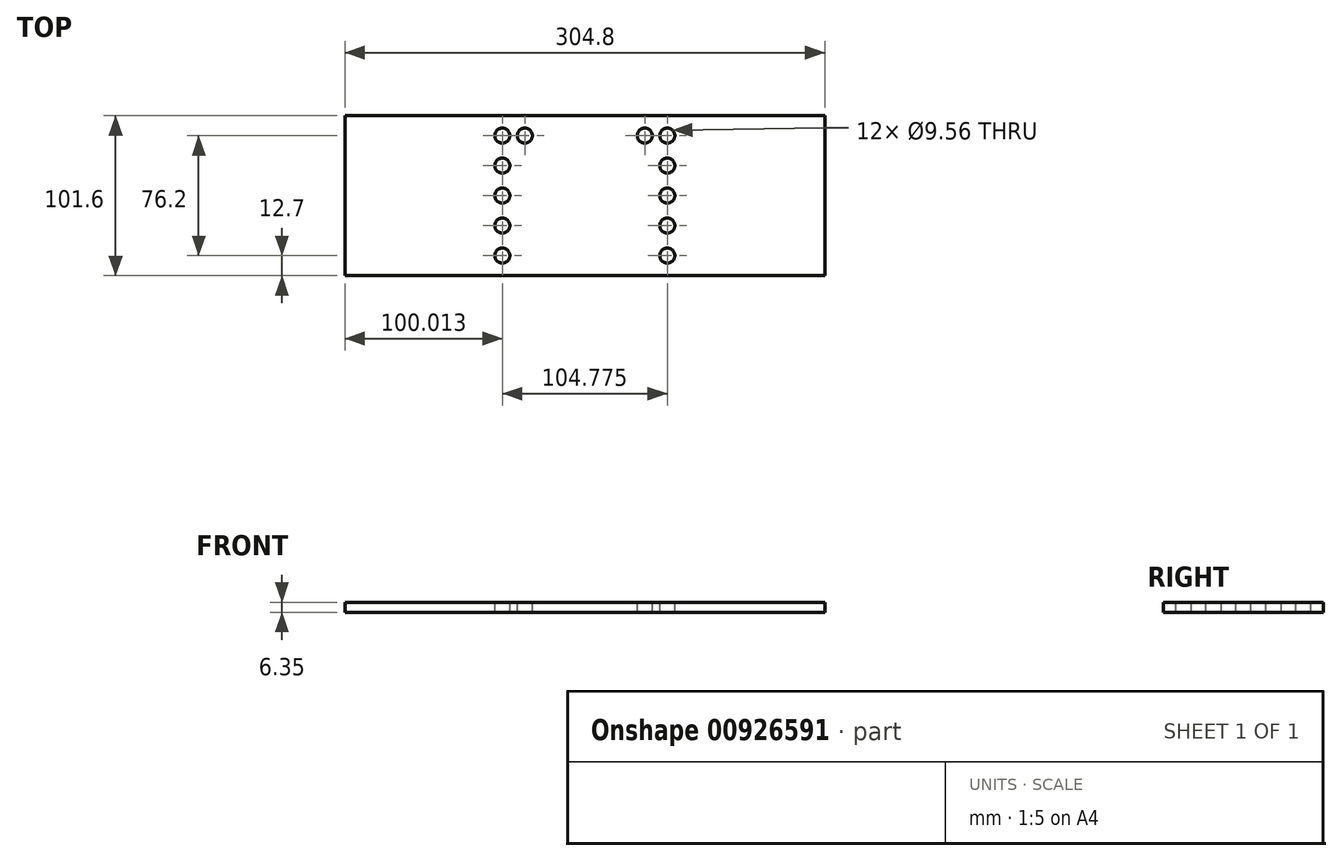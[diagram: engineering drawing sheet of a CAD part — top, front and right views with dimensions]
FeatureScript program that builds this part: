
annotation { "Feature Type Name" : "Feature", "Feature Type Description" : "" }
export const myFeature = defineFeature(function(context is Context, id is Id, definition is map)
    precondition{}
    {
        {
            var Q0;
            Q0=qCreatedBy(makeId("Top.planeOp"),FACE);
            var sketch = newSketch(context, id + "F0", { "sketchPlane" : qUnion([Q0])});
            skLineSegment(sketch, "E0.bottom", {"start": v(-152.4, 50.8) * mm, "end": v(152.4, 50.8) * mm});
            skLineSegment(sketch, "E0.top", {"start": v(-152.4, -50.8) * mm, "end": v(152.4, -50.8) * mm});
            skLineSegment(sketch, "E0.left", {"start": v(-152.4, 50.8) * mm, "end": v(-152.4, -50.8) * mm});
            skLineSegment(sketch, "E0.right", {"start": v(152.4, 50.8) * mm, "end": v(152.4, -50.8) * mm});
            skLineSegment(sketch, "E1", {"start": v(-152.4, 0) * mm, "end": v(0, 0) * mm, "construction": true});
            skLineSegment(sketch, "E2", {"start": v(0, 0) * mm, "end": v(152.4, 0) * mm, "construction": true});
            skLineSegment(sketch, "E3", {"start": v(0, 50.8) * mm, "end": v(0, 0) * mm, "construction": true});
            skLineSegment(sketch, "E4", {"start": v(0, 0) * mm, "end": v(0, -50.8) * mm, "construction": true});
            skSolve(sketch);
        }
        {
            var Q0;
            Q0=qSketchRegion(id+"F0",true);
            extrude(context, id + "F1", {"entities" : qUnion([Q0]), "depth" : 6.35 * mm, "offsetDistance" : 25.4 * mm});
        }
        {
            var Q0;
            Q0=makeQuery(id+"F1.opExtrude","CAP_FACE",FACE,{"disambiguationData":[OSD([sQuery(id+"F0.wireOp",EDGE,"E0.bottom"),sQuery(id+"F0.wireOp",EDGE,"E0.top"),sQuery(id+"F0.wireOp",EDGE,"E0.left"),sQuery(id+"F0.wireOp",EDGE,"E0.right")])],"isStart":false});
            var sketch = newSketch(context, id + "F2", { "sketchPlane" : qUnion([Q0])});
            skCircle(sketch, "E5", {"center": v(-52.39, 38.1) * mm, "radius": 4.78 * mm});
            skCircle(sketch, "E6.0.1.0", {"center": v(-52.39, 19.05) * mm, "radius": 4.78 * mm});
            skCircle(sketch, "E6.1.0.0", {"center": v(52.39, 38.1) * mm, "radius": 4.78 * mm});
            skCircle(sketch, "E6.1.1.0", {"center": v(52.39, 19.05) * mm, "radius": 4.78 * mm});
            skLineSegment(sketch, "E6.direction1", {"start": v(-52.39, 38.1) * mm, "end": v(52.39, 38.1) * mm, "construction": true});
            skLineSegment(sketch, "E6.direction2", {"start": v(-52.39, 38.1) * mm, "end": v(-52.39, 19.05) * mm, "construction": true});
            skLineSegment(sketch, "E7", {"start": v(-52.39, 38.1) * mm, "end": v(-152.4, 38.1) * mm, "construction": true});
            skLineSegment(sketch, "E8", {"start": v(52.39, 38.1) * mm, "end": v(152.4, 38.1) * mm, "construction": true});
            skLineSegment(sketch, "E9", {"start": v(-52.39, 38.1) * mm, "end": v(-52.39, 50.8) * mm, "construction": true});
            skCircle(sketch, "E10.0.0.2", {"center": v(-52.39, 0) * mm, "radius": 4.78 * mm});
            skCircle(sketch, "E10.0.0.3", {"center": v(-52.39, -19.05) * mm, "radius": 4.78 * mm});
            skCircle(sketch, "E10.0.1.2", {"center": v(52.39, 0) * mm, "radius": 4.78 * mm});
            skCircle(sketch, "E10.0.1.3", {"center": v(52.39, -19.05) * mm, "radius": 4.78 * mm});
            skCircle(sketch, "E11.0.0.4", {"center": v(-52.39, -38.1) * mm, "radius": 4.78 * mm});
            skCircle(sketch, "E11.0.1.4", {"center": v(52.39, -38.1) * mm, "radius": 4.78 * mm});
            skLineSegment(sketch, "E12", {"start": v(-52.39, -38.1) * mm, "end": v(-52.39, -50.8) * mm, "construction": true});
            skSolve(sketch);
        }
        {
            var Q0;
            Q0=makeQuery(id+"F2.imprint","IMPRINT",FACE,{"disambiguationData":[TD([[makeQuery(id+"F2.imprint","IMPRINT",EDGE,{"derivedFrom":sQuery(id+"F2.wireOp",EDGE,"E5")}),1.0]])]});
            var Q1;
            Q1=makeQuery(id+"F2.imprint","IMPRINT",FACE,{"disambiguationData":[TD([[makeQuery(id+"F2.imprint","IMPRINT",EDGE,{"derivedFrom":sQuery(id+"F2.wireOp",EDGE,"E6.1.0.0")}),1.0]])]});
            var Q2;
            Q2=makeQuery(id+"F2.imprint","IMPRINT",FACE,{"disambiguationData":[TD([[makeQuery(id+"F2.imprint","IMPRINT",EDGE,{"derivedFrom":sQuery(id+"F2.wireOp",EDGE,"E6.0.1.0")}),1.0]])]});
            var Q3;
            Q3=makeQuery(id+"F2.imprint","IMPRINT",FACE,{"disambiguationData":[TD([[makeQuery(id+"F2.imprint","IMPRINT",EDGE,{"derivedFrom":sQuery(id+"F2.wireOp",EDGE,"E6.1.1.0")}),1.0]])]});
            var Q4;
            Q4=makeQuery(id+"F2.imprint","IMPRINT",FACE,{"disambiguationData":[TD([[makeQuery(id+"F2.imprint","IMPRINT",EDGE,{"derivedFrom":sQuery(id+"F2.wireOp",EDGE,"E10.0.0.2")}),1.0]])]});
            var Q5;
            Q5=makeQuery(id+"F2.imprint","IMPRINT",FACE,{"disambiguationData":[TD([[makeQuery(id+"F2.imprint","IMPRINT",EDGE,{"derivedFrom":sQuery(id+"F2.wireOp",EDGE,"E10.0.0.3")}),1.0]])]});
            var Q6;
            Q6=makeQuery(id+"F2.imprint","IMPRINT",FACE,{"disambiguationData":[TD([[makeQuery(id+"F2.imprint","IMPRINT",EDGE,{"derivedFrom":sQuery(id+"F2.wireOp",EDGE,"E11.0.0.4")}),1.0]])]});
            var Q7;
            Q7=makeQuery(id+"F2.imprint","IMPRINT",FACE,{"disambiguationData":[TD([[makeQuery(id+"F2.imprint","IMPRINT",EDGE,{"derivedFrom":sQuery(id+"F2.wireOp",EDGE,"E10.0.1.2")}),1.0]])]});
            var Q8;
            Q8=makeQuery(id+"F2.imprint","IMPRINT",FACE,{"disambiguationData":[TD([[makeQuery(id+"F2.imprint","IMPRINT",EDGE,{"derivedFrom":sQuery(id+"F2.wireOp",EDGE,"E10.0.1.3")}),1.0]])]});
            var Q9;
            Q9=makeQuery(id+"F2.imprint","IMPRINT",FACE,{"disambiguationData":[TD([[makeQuery(id+"F2.imprint","IMPRINT",EDGE,{"derivedFrom":sQuery(id+"F2.wireOp",EDGE,"E11.0.1.4")}),1.0]])]});
            extrude(context, id + "F3", {"entities" : qUnion([Q0, Q1, Q2, Q3, Q4, Q5, Q6, Q7, Q8, Q9]), "operationType" : NewBodyOperationType.REMOVE, "endBound" : BoundingType.UP_TO_NEXT, "oppositeDirection" : true, "depth" : 25.4 * mm, "offsetDistance" : 25.4 * mm});
        }
        {
            var Q0;
            Q0=makeQuery(id+"F1.opExtrude","CAP_FACE",FACE,{"disambiguationData":[OSD([sQuery(id+"F0.wireOp",EDGE,"E0.bottom"),sQuery(id+"F0.wireOp",EDGE,"E0.top"),sQuery(id+"F0.wireOp",EDGE,"E0.left"),sQuery(id+"F0.wireOp",EDGE,"E0.right")])],"isStart":false});
            var sketch = newSketch(context, id + "F4", { "sketchPlane" : qUnion([Q0])});
            skCircle(sketch, "E13", {"center": v(-38.1, 38.1) * mm, "radius": 4.78 * mm});
            skCircle(sketch, "E14", {"center": v(38.1, 38.1) * mm, "radius": 4.78 * mm});
            skLineSegment(sketch, "E15", {"start": v(-38.1, 38.1) * mm, "end": v(-52.39, 38.1) * mm, "construction": true});
            skLineSegment(sketch, "E16", {"start": v(-38.1, 38.1) * mm, "end": v(0, 38.1) * mm, "construction": true});
            skLineSegment(sketch, "E17", {"start": v(0, 38.1) * mm, "end": v(38.1, 38.1) * mm, "construction": true});
            skSolve(sketch);
        }
        {
            var Q0;
            Q0=makeQuery(id+"F4.imprint","IMPRINT",FACE,{"disambiguationData":[TD([[makeQuery(id+"F4.imprint","IMPRINT",EDGE,{"derivedFrom":sQuery(id+"F4.wireOp",EDGE,"E13")}),1.0]])]});
            var Q1;
            Q1=makeQuery(id+"F4.imprint","IMPRINT",FACE,{"disambiguationData":[TD([[makeQuery(id+"F4.imprint","IMPRINT",EDGE,{"derivedFrom":sQuery(id+"F4.wireOp",EDGE,"E14")}),1.0]])]});
            var Q2;
            Q2=makeQuery(id+"F4.imprint","IMPRINT",FACE,{"disambiguationData":[TD([[makeQuery(id+"F4.imprint","IMPRINT",EDGE,{"derivedFrom":sQuery(id+"F4.wireOp",EDGE,"ZOADDGMz-Aq7V-knPa-nRid-kyLQjFgriDZK")}),1.0]])]});
            var Q3;
            Q3=makeQuery(id+"F4.imprint","IMPRINT",FACE,{"disambiguationData":[TD([[makeQuery(id+"F4.imprint","IMPRINT",EDGE,{"derivedFrom":sQuery(id+"F4.wireOp",EDGE,"dvCPLzuN-FsGb-uNNB-ju4u-8oqW1vlXcgoj")}),1.0]])]});
            extrude(context, id + "F5", {"entities" : qUnion([Q0, Q1, Q2, Q3]), "operationType" : NewBodyOperationType.REMOVE, "endBound" : BoundingType.THROUGH_ALL, "oppositeDirection" : true, "depth" : 25.4 * mm, "offsetDistance" : 25.4 * mm});
        }
    });
